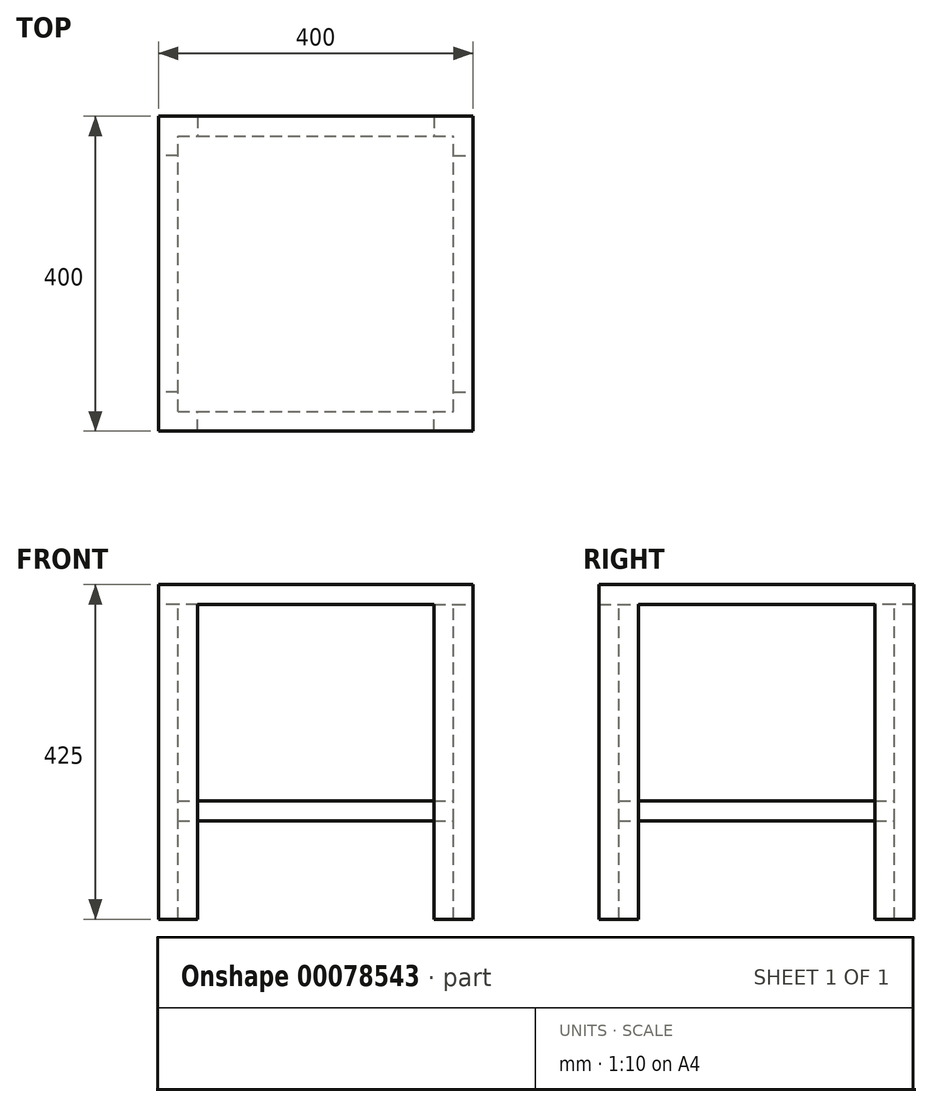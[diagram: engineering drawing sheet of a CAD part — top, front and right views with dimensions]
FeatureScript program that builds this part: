
annotation { "Feature Type Name" : "Feature", "Feature Type Description" : "" }
export const myFeature = defineFeature(function(context is Context, id is Id, definition is map)
    precondition{}
    {
        {
            var Q0;
            Q0=qCreatedBy(makeId("Top.planeOp"),FACE);
            cPlane(context, id + "F0", {"entities" : qUnion([Q0]), "cplaneType" : CPlaneType.OFFSET, "offset" : 150 * mm, "width" : 150 * mm, "height" : 150 * mm});
        }
        {
            var Q0;
            Q0=qCreatedBy(id+"F0.planeOp",FACE);
            var sketch = newSketch(context, id + "F1", { "sketchPlane" : qUnion([Q0])});
            skLineSegment(sketch, "E0.bottom", {"start": v(-200, 200) * mm, "end": v(200, 200) * mm});
            skLineSegment(sketch, "E0.top", {"start": v(-200, -200) * mm, "end": v(200, -200) * mm});
            skLineSegment(sketch, "E0.left", {"start": v(-200, 200) * mm, "end": v(-200, -200) * mm});
            skLineSegment(sketch, "E0.right", {"start": v(200, 200) * mm, "end": v(200, -200) * mm});
            skSolve(sketch);
        }
        {
            var Q0;
            Q0=makeQuery(id+"F1.imprint","IMPRINT",FACE,{"disambiguationData":[TD([[makeQuery(id+"F1.imprint","IMPRINT",EDGE,{"derivedFrom":sQuery(id+"F1.wireOp",EDGE,"E0.bottom")}),-1.0]])]});
            extrude(context, id + "F2", {"entities" : qUnion([Q0]), "oppositeDirection" : true, "depth" : 25 * mm});
        }
        {
            var Q0;
            Q0=makeQuery(id+"F2.opExtrude","CAP_FACE",FACE,{"disambiguationData":[OSD([sQuery(id+"F1.wireOp",EDGE,"E0.bottom"),sQuery(id+"F1.wireOp",EDGE,"E0.top"),sQuery(id+"F1.wireOp",EDGE,"E0.left"),sQuery(id+"F1.wireOp",EDGE,"E0.right")])],"isStart":false});
            var sketch = newSketch(context, id + "F3", { "sketchPlane" : qUnion([Q0])});
            skLineSegment(sketch, "E1", {"start": v(-200, 150) * mm, "end": v(-200, 200) * mm});
            skLineSegment(sketch, "E2", {"start": v(-200, 200) * mm, "end": v(-150, 200) * mm});
            skLineSegment(sketch, "E3", {"start": v(-150, 200) * mm, "end": v(-150, 175) * mm});
            skLineSegment(sketch, "E4", {"start": v(-150, 175) * mm, "end": v(-175, 175) * mm});
            skLineSegment(sketch, "E5", {"start": v(-175, 175) * mm, "end": v(-175, 150) * mm});
            skLineSegment(sketch, "E6", {"start": v(-175, 150) * mm, "end": v(-200, 150) * mm});
            skLineSegment(sketch, "E7.MirrorCS", {"start": v(175, 175) * mm, "end": v(175, 150) * mm});
            skLineSegment(sketch, "E8.MirrorCS", {"start": v(200, 200) * mm, "end": v(150, 200) * mm});
            skLineSegment(sketch, "E9.MirrorCS", {"start": v(200, 150) * mm, "end": v(200, 200) * mm});
            skLineSegment(sketch, "E10.MirrorCS", {"start": v(150, 200) * mm, "end": v(150, 175) * mm});
            skLineSegment(sketch, "E11.MirrorCS", {"start": v(150, 175) * mm, "end": v(175, 175) * mm});
            skLineSegment(sketch, "E12.MirrorCS", {"start": v(175, 150) * mm, "end": v(200, 150) * mm});
            skLineSegment(sketch, "E13.MirrorCS", {"start": v(-175, -175) * mm, "end": v(-175, -150) * mm});
            skLineSegment(sketch, "E14.MirrorCS", {"start": v(-150, -175) * mm, "end": v(-175, -175) * mm});
            skLineSegment(sketch, "E15.MirrorCS", {"start": v(-150, -200) * mm, "end": v(-150, -175) * mm});
            skLineSegment(sketch, "E16.MirrorCS", {"start": v(-200, -200) * mm, "end": v(-150, -200) * mm});
            skLineSegment(sketch, "E17.MirrorCS", {"start": v(-200, -150) * mm, "end": v(-200, -200) * mm});
            skLineSegment(sketch, "E18.MirrorCS", {"start": v(-175, -150) * mm, "end": v(-200, -150) * mm});
            skLineSegment(sketch, "E19.MirrorCS", {"start": v(175, -175) * mm, "end": v(175, -150) * mm});
            skLineSegment(sketch, "E20.MirrorCS", {"start": v(200, -200) * mm, "end": v(150, -200) * mm});
            skLineSegment(sketch, "E21.MirrorCS", {"start": v(200, -150) * mm, "end": v(200, -200) * mm});
            skLineSegment(sketch, "E22.MirrorCS", {"start": v(150, -200) * mm, "end": v(150, -175) * mm});
            skLineSegment(sketch, "E23.MirrorCS", {"start": v(175, -150) * mm, "end": v(200, -150) * mm});
            skLineSegment(sketch, "E24.MirrorCS", {"start": v(150, -175) * mm, "end": v(175, -175) * mm});
            skSolve(sketch);
        }
        {
            var Q0;
            Q0 = qSketchRegion(id + "F3", true);
            extrude(context, id + "F4", {"entities" : qUnion([Q0]), "operationType" : NewBodyOperationType.ADD, "depth" : 400 * mm});
        }
        {
            var Q0;
            Q0=qCreatedBy(makeId("Top.planeOp"),FACE);
            cPlane(context, id + "F5", {"entities" : qUnion([Q0]), "cplaneType" : CPlaneType.OFFSET, "offset" : 150 * mm, "oppositeDirection" : true, "width" : 150 * mm, "height" : 150 * mm});
        }
        {
            var Q0;
            Q0=qCreatedBy(id+"F5.planeOp",FACE);
            var sketch = newSketch(context, id + "F6", { "sketchPlane" : qUnion([Q0])});
            skLineSegment(sketch, "E25.bottom", {"start": v(-175, -175) * mm, "end": v(175, -175) * mm});
            skLineSegment(sketch, "E25.top", {"start": v(-175, 175) * mm, "end": v(175, 175) * mm});
            skLineSegment(sketch, "E25.left", {"start": v(-175, -175) * mm, "end": v(-175, 175) * mm});
            skLineSegment(sketch, "E25.right", {"start": v(175, -175) * mm, "end": v(175, 175) * mm});
            skSolve(sketch);
        }
        {
            var Q0;
            Q0=makeQuery(id+"F6.imprint","IMPRINT",FACE,{"disambiguationData":[TD([[makeQuery(id+"F6.imprint","IMPRINT",EDGE,{"derivedFrom":sQuery(id+"F6.wireOp",EDGE,"E25.bottom")}),1.0]])]});
            extrude(context, id + "F7", {"entities" : qUnion([Q0]), "operationType" : NewBodyOperationType.ADD, "depth" : 25 * mm});
        }
    });
